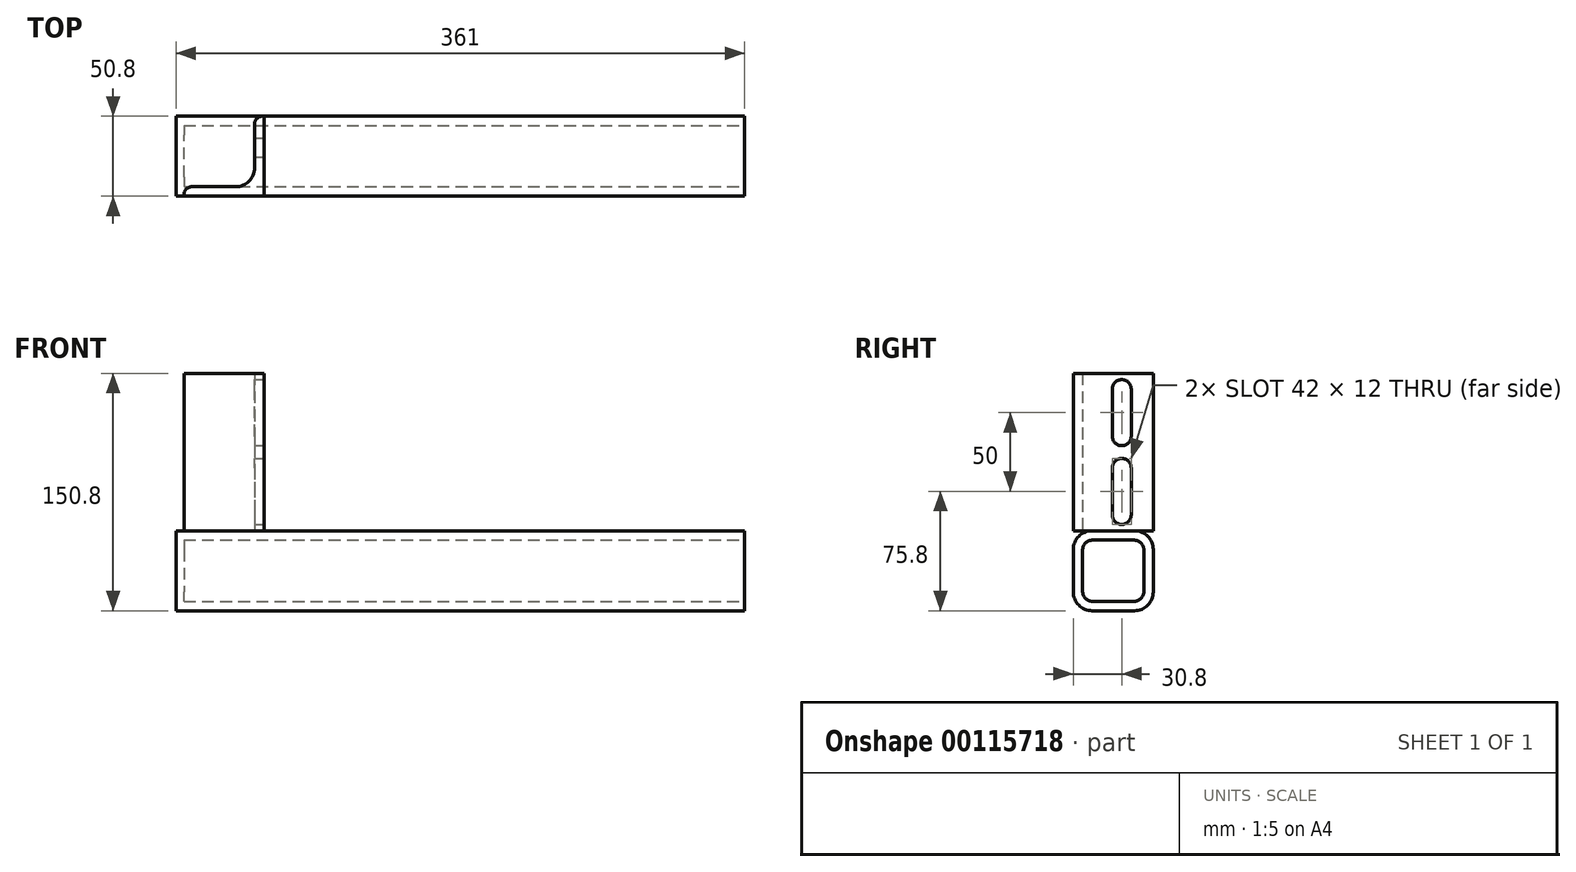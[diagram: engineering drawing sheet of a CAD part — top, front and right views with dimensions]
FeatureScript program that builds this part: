
annotation { "Feature Type Name" : "Feature", "Feature Type Description" : "" }
export const myFeature = defineFeature(function(context is Context, id is Id, definition is map)
    precondition{}
    {
        {
            var Q0;
            Q0=qCreatedBy(makeId("Right.planeOp"),FACE);
            var sketch = newSketch(context, id + "F0", { "sketchPlane" : qUnion([Q0])});
            skLineSegment(sketch, "E0.bottom", {"start": v(-13.4, 25.4) * mm, "end": v(13.4, 25.4) * mm});
            skLineSegment(sketch, "E0.top", {"start": v(-13.4, -25.4) * mm, "end": v(13.4, -25.4) * mm});
            skLineSegment(sketch, "E0.left", {"start": v(-25.4, 13.4) * mm, "end": v(-25.4, -13.4) * mm});
            skLineSegment(sketch, "E0.right", {"start": v(25.4, 13.4) * mm, "end": v(25.4, -13.4) * mm});
            skPoint(sketch, "E0.middle", {"position": v(0, 0) * mm});
            skPoint(sketch, "E1.visualSharp", {"position": v(-25.4, 25.4) * mm});
            skArc(sketch, "E1.filletArc", {"start": v(-13.4, 25.4) * mm, "mid": v(-21.89, 21.89) * mm, "end": v(-25.4, 13.4) * mm});
            skPoint(sketch, "E2.visualSharp", {"position": v(25.4, 25.4) * mm});
            skArc(sketch, "E2.filletArc", {"start": v(25.4, 13.4) * mm, "mid": v(21.89, 21.89) * mm, "end": v(13.4, 25.4) * mm});
            skPoint(sketch, "E3.visualSharp", {"position": v(25.4, -25.4) * mm});
            skArc(sketch, "E3.filletArc", {"start": v(13.4, -25.4) * mm, "mid": v(21.89, -21.89) * mm, "end": v(25.4, -13.4) * mm});
            skPoint(sketch, "E4.visualSharp", {"position": v(-25.4, -25.4) * mm});
            skArc(sketch, "E4.filletArc", {"start": v(-25.4, -13.4) * mm, "mid": v(-21.89, -21.89) * mm, "end": v(-13.4, -25.4) * mm});
            skArc(sketch, "E5.0", {"start": v(-13.4, 19.4) * mm, "mid": v(-17.64, 17.64) * mm, "end": v(-19.4, 13.4) * mm});
            skLineSegment(sketch, "E5.1", {"start": v(-19.4, 13.4) * mm, "end": v(-19.4, -13.4) * mm});
            skLineSegment(sketch, "E5.2", {"start": v(-13.4, 19.4) * mm, "end": v(13.4, 19.4) * mm});
            skArc(sketch, "E5.3", {"start": v(-19.4, -13.4) * mm, "mid": v(-17.64, -17.64) * mm, "end": v(-13.4, -19.4) * mm});
            skArc(sketch, "E5.4", {"start": v(19.4, 13.4) * mm, "mid": v(17.64, 17.64) * mm, "end": v(13.4, 19.4) * mm});
            skLineSegment(sketch, "E5.5", {"start": v(19.4, 13.4) * mm, "end": v(19.4, -13.4) * mm});
            skArc(sketch, "E5.6", {"start": v(13.4, -19.4) * mm, "mid": v(17.64, -17.64) * mm, "end": v(19.4, -13.4) * mm});
            skLineSegment(sketch, "E5.7", {"start": v(-13.4, -19.4) * mm, "end": v(13.4, -19.4) * mm});
            skSolve(sketch);
        }
        {
            var Q0;
            Q0 = qSketchRegion(id + "F0", true);
            extrude(context, id + "F1", {"entities" : qUnion([Q0]), "oppositeDirection" : true, "depth" : 356 * mm});
        }
        {
            var Q0;
            Q0=makeQuery(id+"F1.opExtrude","SWEPT_FACE",FACE,{"disambiguationData":[OSD([sQuery(id+"F0.wireOp",EDGE,"E0.bottom")])]});
            var sketch = newSketch(context, id + "F2", { "sketchPlane" : qUnion([Q0])});
            skLineSegment(sketch, "E6.0", {"start": v(-305.2, -25.4) * mm, "end": v(-305.2, 13.4) * mm, "construction": true});
            skLineSegment(sketch, "E7.bottom", {"start": v(-305.2, -25.4) * mm, "end": v(-356, -25.4) * mm});
            skLineSegment(sketch, "E7.top", {"start": v(-305.2, 25.4) * mm, "end": v(-306.2, 25.4) * mm});
            skLineSegment(sketch, "E7.left", {"start": v(-305.2, -25.4) * mm, "end": v(-305.2, 25.4) * mm});
            skLineSegment(sketch, "E7.right", {"start": v(-356, -25.4) * mm, "end": v(-356, -24.4) * mm});
            skLineSegment(sketch, "E8.0", {"start": v(-311.2, -7.4) * mm, "end": v(-311.2, 20.4) * mm});
            skLineSegment(sketch, "E9.0", {"start": v(-323.2, -19.4) * mm, "end": v(-351, -19.4) * mm});
            skArc(sketch, "E10.filletArc", {"start": v(-323.2, -19.4) * mm, "mid": v(-314.71, -15.89) * mm, "end": v(-311.2, -7.4) * mm});
            skPoint(sketch, "E11.0.end.orphan", {"position": v(-356, 13.4) * mm});
            skPoint(sketch, "E11.0.start.orphan", {"position": v(-356, -13.4) * mm});
            skLineSegment(sketch, "E12.trimOffspring", {"start": v(-356, -13.4) * mm, "end": v(-356, 13.4) * mm});
            skPoint(sketch, "E13.visualSharp", {"position": v(-311.2, 25.4) * mm});
            skArc(sketch, "E13.filletArc", {"start": v(-306.2, 25.4) * mm, "mid": v(-309.74, 23.94) * mm, "end": v(-311.2, 20.4) * mm});
            skPoint(sketch, "E14.visualSharp", {"position": v(-356, -19.4) * mm});
            skArc(sketch, "E14.filletArc", {"start": v(-351, -19.4) * mm, "mid": v(-354.54, -20.86) * mm, "end": v(-356, -24.4) * mm});
            skSolve(sketch);
        }
        {
            var Q0;
            {var subQ2=sQuery(id+"F2.wireOp",EDGE,"E7.bottom");Q0=makeQuery(id+"F2.imprint","IMPRINT",FACE,{"disambiguationData":[TD([[makeQuery(id+"F2.imprint","IMPRINT",EDGE,{"derivedFrom":subQ2}),-1.0]])]});}
            var Q1;
            {var subQ4=sQuery(id+"F2.wireOp",EDGE,"E10.filletArc");var subQ6=sQuery(id+"F2.wireOp",EDGE,"E8.0");var subQ7=makeQuery(id+"F2.imprint","INTERSECT",VERTEX,{"derivedFrom":[subQ6,subQ4]});Q1=makeQuery(id+"F2.imprint","IMPRINT",FACE,{"disambiguationData":[TD([[makeQuery(id+"F2.imprint","IMPRINT",EDGE,{"disambiguationData":[TD([[subQ7,-1.0]])],"derivedFrom":subQ6}),-1.0]])]});}
            var Q2;
            {var subQ5=sQuery(id+"F2.wireOp",EDGE,"E7.top");Q2=makeQuery(id+"F2.imprint","IMPRINT",FACE,{"disambiguationData":[TD([[makeQuery(id+"F2.imprint","IMPRINT",EDGE,{"derivedFrom":subQ5}),1.0]])]});}
            extrude(context, id + "F3", {"entities" : qUnion([Q0, Q1, Q2]), "depth" : 100 * mm});
        }
        {
            var Q0;
            Q0=makeQuery(id+"F3.opExtrude","SWEPT_FACE",FACE,{"disambiguationData":[OSD([sQuery(id+"F2.wireOp",EDGE,"E7.left")])]});
            var sketch = newSketch(context, id + "F4", { "sketchPlane" : qUnion([Q0])});
            skLineSegment(sketch, "E15.0", {"start": v(25.4, 125.4) * mm, "end": v(25.4, 25.4) * mm, "construction": true});
            skLineSegment(sketch, "E16.0", {"start": v(5.4, 125.4) * mm, "end": v(5.4, 25.4) * mm, "construction": true});
            skLineSegment(sketch, "E17.0", {"start": v(-25.4, 125.4) * mm, "end": v(25.4, 125.4) * mm, "construction": true});
            skLineSegment(sketch, "E18.0", {"start": v(-25.4, 75.4) * mm, "end": v(25.4, 75.4) * mm, "construction": true});
            skLineSegment(sketch, "E19.0", {"start": v(-25.4, 100.4) * mm, "end": v(25.4, 100.4) * mm, "construction": true});
            skLineSegment(sketch, "E20.0", {"start": v(-25.4, 85.4) * mm, "end": v(25.4, 85.4) * mm, "construction": true});
            skLineSegment(sketch, "E21.0", {"start": v(-25.4, 115.4) * mm, "end": v(25.4, 115.4) * mm, "construction": true});
            skLineSegment(sketch, "E22", {"start": v(5.4, 115.4) * mm, "end": v(5.4, 85.4) * mm});
            skArc(sketch, "E23.0.startCap", {"start": v(-0.6, 115.4) * mm, "mid": v(5.4, 121.4) * mm, "end": v(11.4, 115.4) * mm});
            skArc(sketch, "E23.0.endCap", {"start": v(11.4, 85.4) * mm, "mid": v(5.4, 79.4) * mm, "end": v(-0.6, 85.4) * mm});
            skLineSegment(sketch, "E23.0.left", {"start": v(11.4, 115.4) * mm, "end": v(11.4, 85.4) * mm});
            skLineSegment(sketch, "E23.0.right", {"start": v(-0.6, 115.4) * mm, "end": v(-0.6, 85.4) * mm});
            skLineSegment(sketch, "E24.MirrorCS", {"start": v(-0.6, 35.4) * mm, "end": v(-0.6, 65.4) * mm});
            skLineSegment(sketch, "E25.MirrorCS", {"start": v(11.4, 35.4) * mm, "end": v(11.4, 65.4) * mm});
            skArc(sketch, "E26.MirrorCS", {"start": v(11.4, 65.4) * mm, "mid": v(5.4, 71.4) * mm, "end": v(-0.6, 65.4) * mm});
            skArc(sketch, "E27.MirrorCS", {"start": v(-0.6, 35.4) * mm, "mid": v(5.4, 29.4) * mm, "end": v(11.4, 35.4) * mm});
            skLineSegment(sketch, "E28.MirrorCS", {"start": v(5.4, 35.4) * mm, "end": v(5.4, 65.4) * mm});
            skSolve(sketch);
        }
        {
            var Q0;
            Q0 = qSketchRegion(id + "F4", true);
            extrude(context, id + "F5", {"entities" : qUnion([Q0]), "operationType" : NewBodyOperationType.REMOVE, "endBound" : BoundingType.THROUGH_ALL, "oppositeDirection" : true, "depth" : 25 * mm});
        }
        {
            var Q0;
            Q0=makeQuery(id+"F1.opExtrude","CAP_FACE",FACE,{"disambiguationData":[OSD([sQuery(id+"F0.wireOp",EDGE,"E0.bottom"),sQuery(id+"F0.wireOp",EDGE,"E0.top"),sQuery(id+"F0.wireOp",EDGE,"E0.left"),sQuery(id+"F0.wireOp",EDGE,"E0.right"),sQuery(id+"F0.wireOp",EDGE,"E1.filletArc"),sQuery(id+"F0.wireOp",EDGE,"E2.filletArc"),sQuery(id+"F0.wireOp",EDGE,"E3.filletArc"),sQuery(id+"F0.wireOp",EDGE,"E4.filletArc"),sQuery(id+"F0.wireOp",EDGE,"E5.0"),sQuery(id+"F0.wireOp",EDGE,"E5.1"),sQuery(id+"F0.wireOp",EDGE,"E5.2"),sQuery(id+"F0.wireOp",EDGE,"E5.3"),sQuery(id+"F0.wireOp",EDGE,"E5.4"),sQuery(id+"F0.wireOp",EDGE,"E5.5"),sQuery(id+"F0.wireOp",EDGE,"E5.6"),sQuery(id+"F0.wireOp",EDGE,"E5.7")])],"isStart":false});
            var sketch = newSketch(context, id + "F6", { "sketchPlane" : qUnion([Q0])});
            skLineSegment(sketch, "E29.0", {"start": v(-25.4, 13.4) * mm, "end": v(-25.4, -13.4) * mm});
            skArc(sketch, "E30.0", {"start": v(-25.4, 13.4) * mm, "mid": v(-21.89, 21.89) * mm, "end": v(-13.4, 25.4) * mm});
            skLineSegment(sketch, "E31.0", {"start": v(13.4, 25.4) * mm, "end": v(-13.4, 25.4) * mm});
            skArc(sketch, "E32.0", {"start": v(13.4, 25.4) * mm, "mid": v(21.89, 21.89) * mm, "end": v(25.4, 13.4) * mm});
            skLineSegment(sketch, "E33.0", {"start": v(25.4, 13.4) * mm, "end": v(25.4, -13.4) * mm});
            skArc(sketch, "E34.0", {"start": v(25.4, -13.4) * mm, "mid": v(21.89, -21.89) * mm, "end": v(13.4, -25.4) * mm});
            skLineSegment(sketch, "E35.0", {"start": v(13.4, -25.4) * mm, "end": v(-13.4, -25.4) * mm});
            skArc(sketch, "E36.0", {"start": v(-13.4, -25.4) * mm, "mid": v(-21.89, -21.89) * mm, "end": v(-25.4, -13.4) * mm});
            skSolve(sketch);
        }
        {
            var Q0;
            Q0 = qSketchRegion(id + "F6", true);
            extrude(context, id + "F7", {"entities" : qUnion([Q0]), "operationType" : NewBodyOperationType.ADD, "depth" : 5 * mm});
        }
    });
